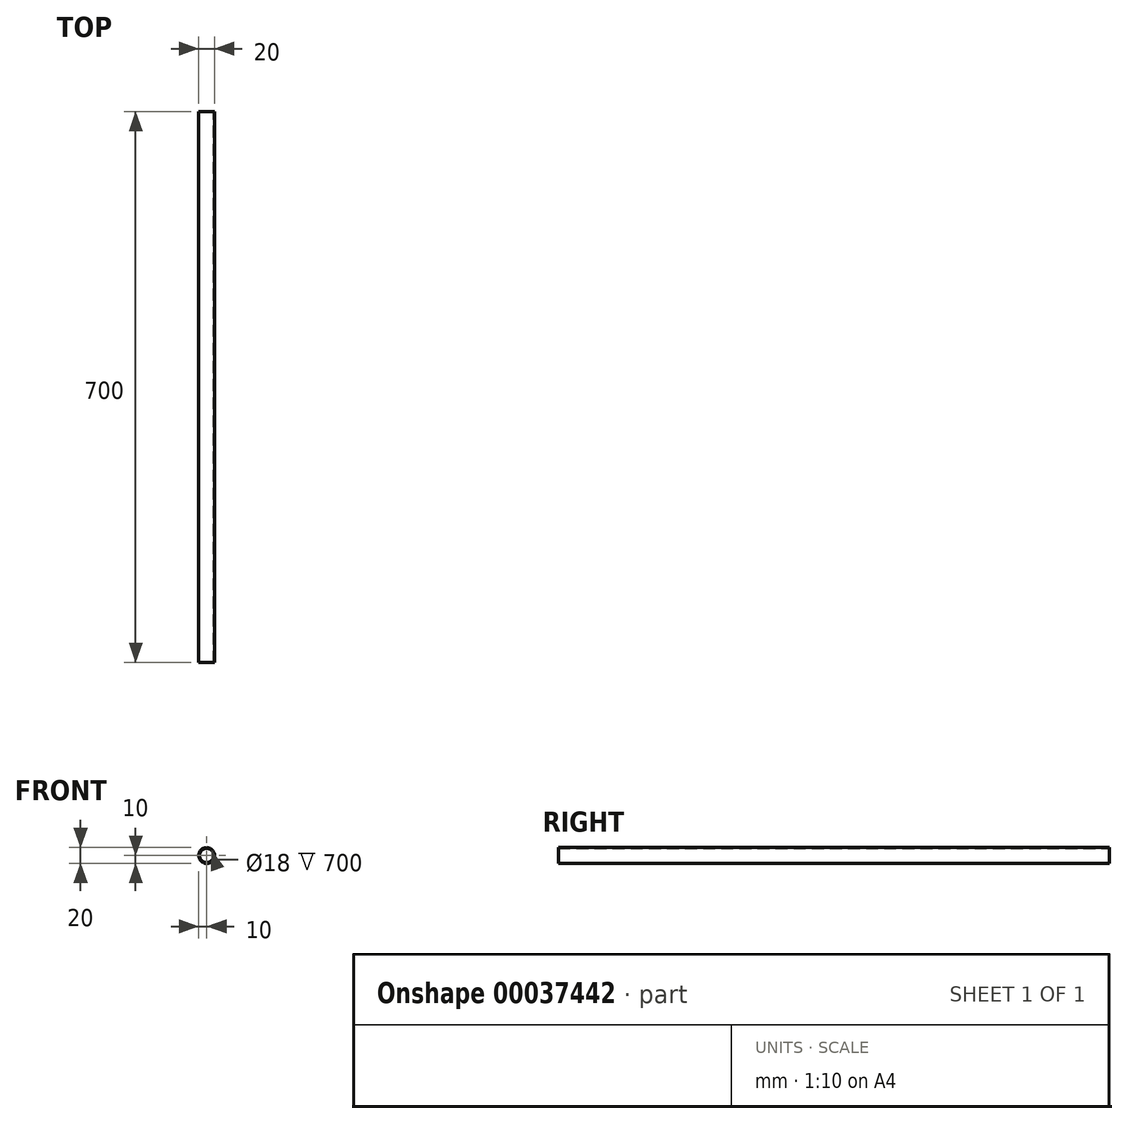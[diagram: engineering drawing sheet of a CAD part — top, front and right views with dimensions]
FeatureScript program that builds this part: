
annotation { "Feature Type Name" : "Feature", "Feature Type Description" : "" }
export const myFeature = defineFeature(function(context is Context, id is Id, definition is map)
    precondition{}
    {
        {
            var Q0;
            Q0=qCreatedBy(makeId("Front.planeOp"),FACE);
            var sketch = newSketch(context, id + "F0", { "sketchPlane" : qUnion([Q0])});
            skCircle(sketch, "E0", {"center": v(0, 0) * mm, "radius": 10 * mm});
            skCircle(sketch, "E1.0", {"center": v(0, 0) * mm, "radius": 9 * mm});
            skSolve(sketch);
        }
        {
            var Q0;
            Q0 = qSketchRegion(id + "F0", true);
            extrude(context, id + "F1", {"entities" : qUnion([Q0]), "depth" : 700 * mm});
        }
    });
